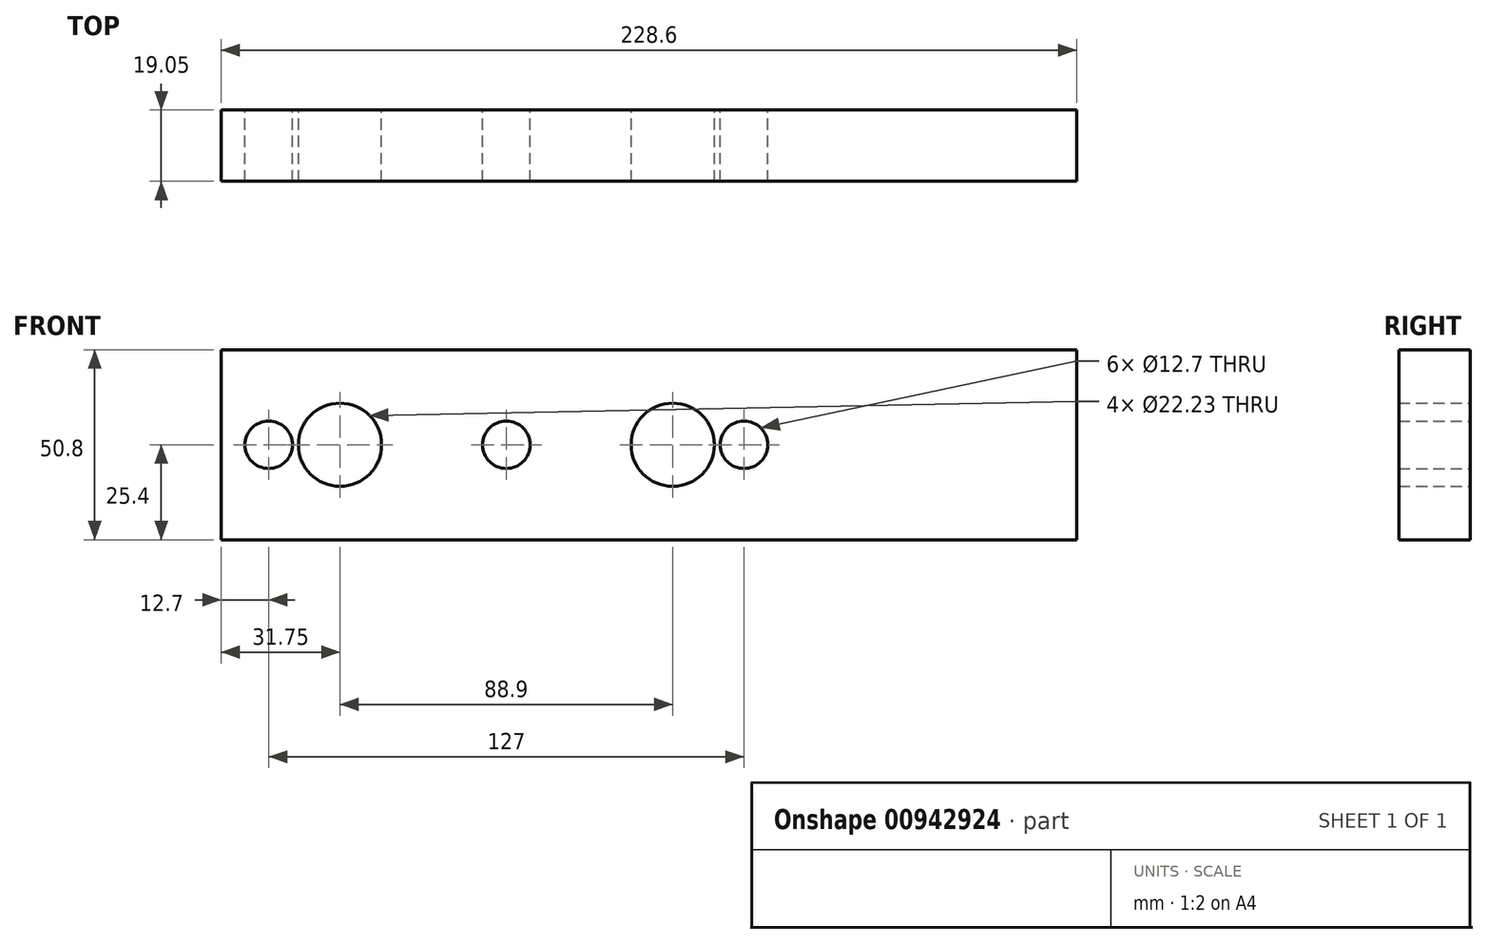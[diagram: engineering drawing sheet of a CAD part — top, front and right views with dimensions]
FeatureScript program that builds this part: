
annotation { "Feature Type Name" : "Feature", "Feature Type Description" : "" }
export const myFeature = defineFeature(function(context is Context, id is Id, definition is map)
    precondition{}
    {
        {
            var Q0;
            Q0=qCreatedBy(makeId("Front.planeOp"),FACE);
            var sketch = newSketch(context, id + "F0", { "sketchPlane" : qUnion([Q0])});
            skLineSegment(sketch, "E0.bottom", {"start": v(0, 0) * mm, "end": v(228.6, 0) * mm});
            skLineSegment(sketch, "E0.top", {"start": v(0, 50.8) * mm, "end": v(228.6, 50.8) * mm});
            skLineSegment(sketch, "E0.left", {"start": v(0, 0) * mm, "end": v(0, 50.8) * mm});
            skLineSegment(sketch, "E0.right", {"start": v(228.6, 0) * mm, "end": v(228.6, 50.8) * mm});
            skCircle(sketch, "E1", {"center": v(12.7, 25.4) * mm, "radius": 6.35 * mm});
            skCircle(sketch, "E2", {"center": v(76.2, 25.4) * mm, "radius": 6.35 * mm});
            skCircle(sketch, "E3", {"center": v(139.7, 25.4) * mm, "radius": 6.35 * mm});
            skLineSegment(sketch, "E4", {"start": v(0, 25.4) * mm, "end": v(228.6, 25.4) * mm, "construction": true});
            skCircle(sketch, "E5", {"center": v(31.75, 25.4) * mm, "radius": 11.11 * mm});
            skCircle(sketch, "E6", {"center": v(120.65, 25.4) * mm, "radius": 11.11 * mm});
            skSolve(sketch);
        }
        {
            var Q0;
            Q0=makeQuery(id+"F0.imprint","IMPRINT",FACE,{"disambiguationData":[TD([[makeQuery(id+"F0.imprint","IMPRINT",EDGE,{"derivedFrom":sQuery(id+"F0.wireOp",EDGE,"E0.bottom")}),1.0]])]});
            extrude(context, id + "F1", {"entities" : qUnion([Q0]), "depth" : 25.4 * 3 / 4 * mm, "offsetDistance" : 25 * mm});
        }
    });
